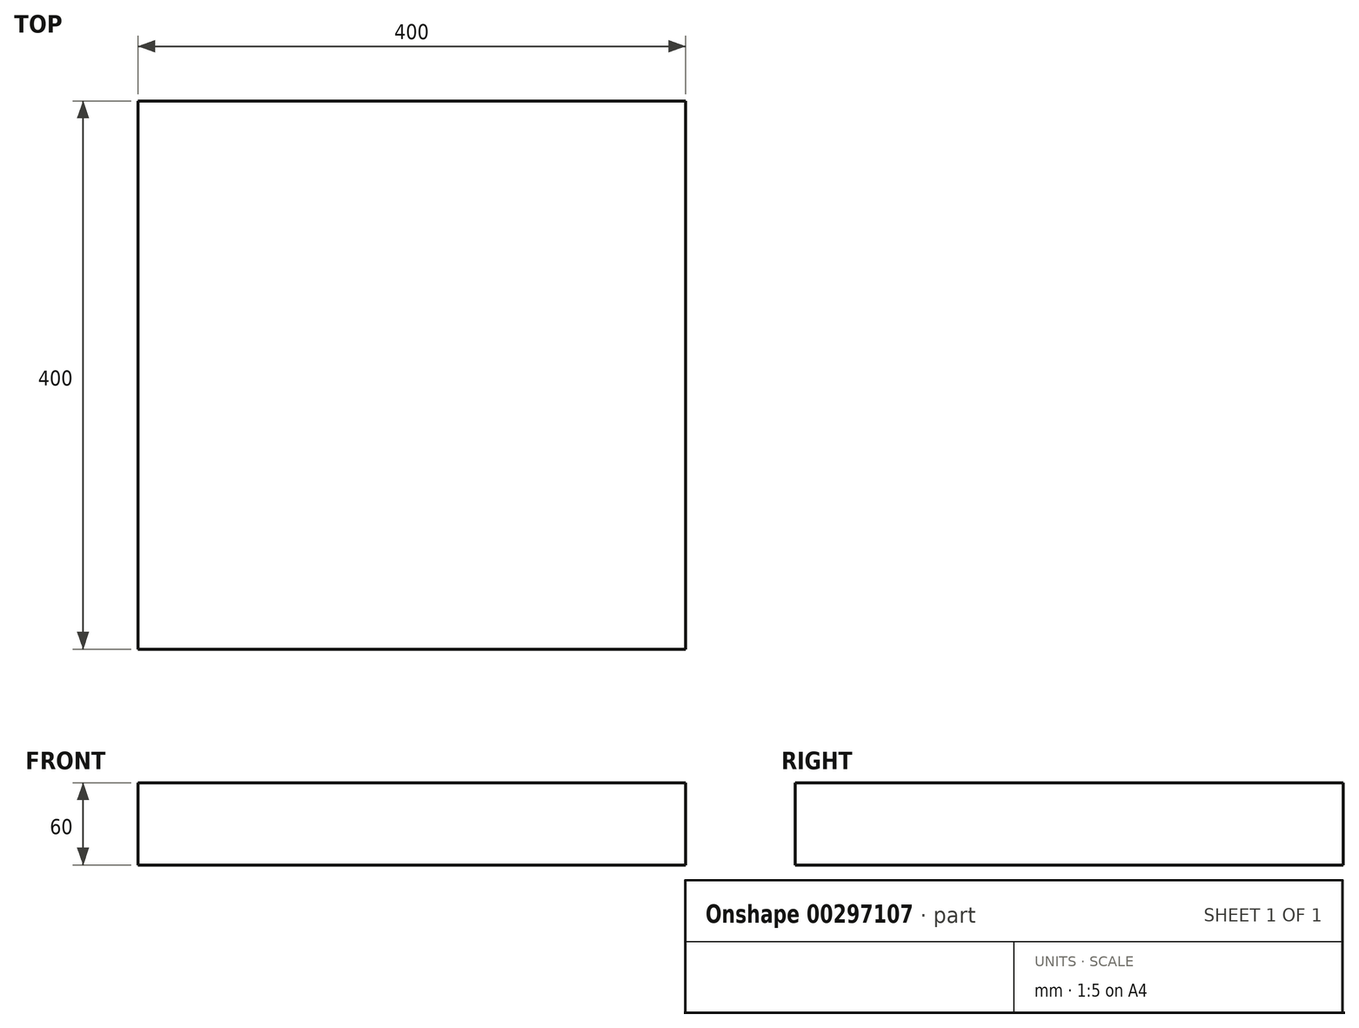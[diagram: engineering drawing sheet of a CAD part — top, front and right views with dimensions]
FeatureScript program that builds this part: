
annotation { "Feature Type Name" : "Feature", "Feature Type Description" : "" }
export const myFeature = defineFeature(function(context is Context, id is Id, definition is map)
    precondition{}
    {
        {
            var Q0;
            Q0=qCreatedBy(makeId("Top.planeOp"),FACE);
            var sketch = newSketch(context, id + "F0", { "sketchPlane" : qUnion([Q0])});
            skLineSegment(sketch, "E0.bottom", {"start": v(-200, 200) * mm, "end": v(200, 200) * mm});
            skLineSegment(sketch, "E0.top", {"start": v(-200, -200) * mm, "end": v(200, -200) * mm});
            skLineSegment(sketch, "E0.left", {"start": v(-200, 200) * mm, "end": v(-200, -200) * mm});
            skLineSegment(sketch, "E0.right", {"start": v(200, 200) * mm, "end": v(200, -200) * mm});
            skPoint(sketch, "E0.middle", {"position": v(0, 0) * mm});
            skSolve(sketch);
        }
        {
            var Q0;
            Q0=makeQuery(id+"F0.imprint","IMPRINT",FACE,{"disambiguationData":[TD([[makeQuery(id+"F0.imprint","IMPRINT",EDGE,{"derivedFrom":sQuery(id+"F0.wireOp",EDGE,"E0.bottom")}),-1.0]])]});
            extrude(context, id + "F1", {"entities" : qUnion([Q0]), "depth" : 60 * mm});
        }
    });
